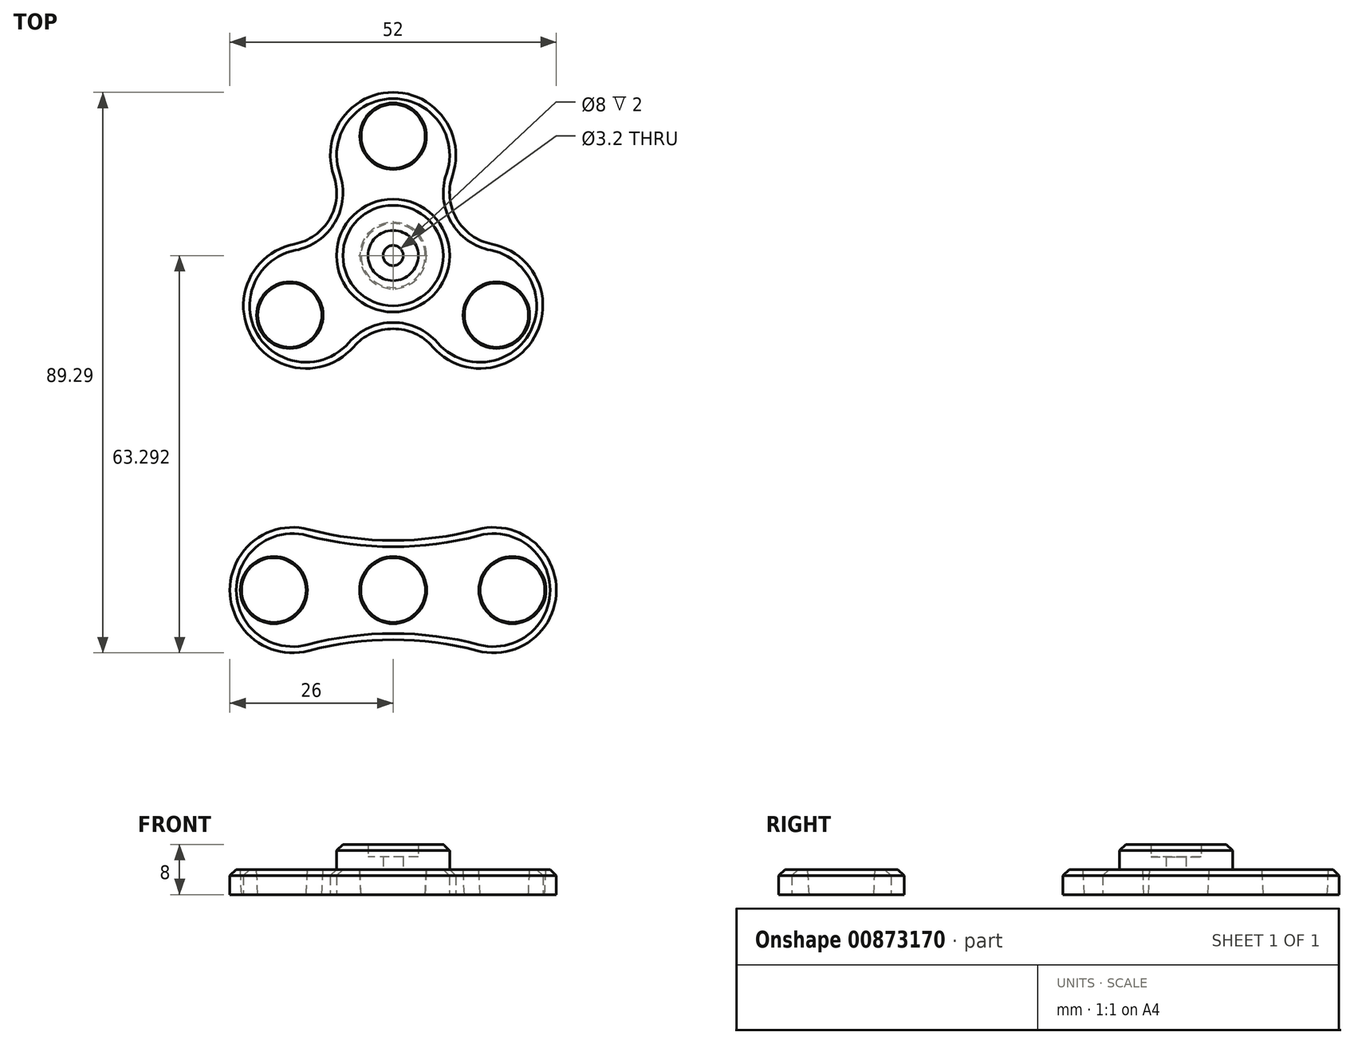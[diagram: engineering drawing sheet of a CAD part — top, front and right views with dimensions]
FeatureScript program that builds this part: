
annotation { "Feature Type Name" : "Feature", "Feature Type Description" : "" }
export const myFeature = defineFeature(function(context is Context, id is Id, definition is map)
    precondition{}
    {
        {
            var Q0;
            Q0=qCreatedBy(makeId("Top.planeOp"),FACE);
            var sketch = newSketch(context, id + "F0", { "sketchPlane" : qUnion([Q0])});
            skCircle(sketch, "E0", {"center": v(0, 0) * mm, "radius": 5.15 * mm});
            skCircle(sketch, "E1", {"center": v(0, 0) * mm, "radius": 30 * mm, "construction": true});
            skCircle(sketch, "E2", {"center": v(0, 0) * mm, "radius": 16 * mm, "construction": true});
            skCircle(sketch, "E3", {"center": v(-16, 0) * mm, "radius": 10 * mm});
            skCircle(sketch, "E4", {"center": v(16, 0) * mm, "radius": 10 * mm});
            skCircle(sketch, "E5", {"center": v(0, 0) * mm, "radius": 60 * mm, "construction": true});
            skArc(sketch, "E6", {"start": v(-46.93, 37.38) * mm, "mid": v(0, 7.9) * mm, "end": v(46.93, 37.38) * mm});
            skPoint(sketch, "E7.center.orphan", {"position": v(0, -60) * mm});
            skCircle(sketch, "E8", {"center": v(0, 0) * mm, "radius": 19 * mm, "construction": true});
            skCircle(sketch, "E9", {"center": v(-19, 0) * mm, "radius": 5.15 * mm});
            skCircle(sketch, "E10", {"center": v(19, 0) * mm, "radius": 5.15 * mm});
            skArc(sketch, "E11.MirrorCS", {"start": v(-46.93, -37.38) * mm, "mid": v(0, -7.9) * mm, "end": v(46.93, -37.38) * mm});
            skSolve(sketch);
        }
        {
            var Q0;
            Q0=makeQuery(id+"F0.imprint","IMPRINT",FACE,{"disambiguationData":[TD([[makeQuery(id+"F0.imprint","IMPRINT",EDGE,{"derivedFrom":sQuery(id+"F0.wireOp",EDGE,"kzVZ2nqX-SIj2-GYyN-E4sG-fJVBGGT2UGiY")}),-1.0]])]});
            var Q1;
            Q1=makeQuery(id+"F0.imprint","IMPRINT",FACE,{"disambiguationData":[TD([[makeQuery(id+"F0.imprint","IMPRINT",EDGE,{"derivedFrom":sQuery(id+"F0.wireOp",EDGE,"E0")}),-1.0]])]});
            var Q2;
            Q2=makeQuery(id+"F0.imprint","IMPRINT",FACE,{"disambiguationData":[TD([[makeQuery(id+"F0.imprint","IMPRINT",EDGE,{"derivedFrom":sQuery(id+"F0.wireOp",EDGE,"PU9XcHGf-sTf9-tFIX-0EHb-OrcDif7mutCM")}),-1.0]])]});
            var Q3;
            Q3=makeQuery(id+"F0.imprint","IMPRINT",FACE,{"disambiguationData":[TD([[makeQuery(id+"F0.imprint","IMPRINT",EDGE,{"derivedFrom":sQuery(id+"F0.wireOp",EDGE,"E9")}),-1.0]])]});
            var Q4;
            Q4=makeQuery(id+"F0.imprint","IMPRINT",FACE,{"disambiguationData":[TD([[makeQuery(id+"F0.imprint","IMPRINT",EDGE,{"derivedFrom":sQuery(id+"F0.wireOp",EDGE,"E10")}),-1.0]])]});
            extrude(context, id + "F1", {"entities" : qUnion([Q0, Q1, Q2, Q3, Q4]), "depth" : 4 * mm, "offsetDistance" : 25 * mm});
        }
        {
            var Q0;
            Q0=makeQuery(id+"F1.opExtrude","CAP_EDGE",EDGE,{"disambiguationData":[OSD([sQuery(id+"F0.wireOp",EDGE,"9445dba6-547d-4354-881b-b922ac0d47a12")])],"isStart":false});
            var Q1;
            Q1=makeQuery(id+"F1.opExtrude","CAP_EDGE",EDGE,{"disambiguationData":[OSD([sQuery(id+"F0.wireOp",EDGE,"E11.MirrorCS")])],"isStart":false});
            chamfer(context, id + "F2", {"entities" : qUnion([Q0, Q1]), "width" : 1 * mm, "tangentPropagation" : true});
        }
        {
            var Q0;
            Q0=qCreatedBy(makeId("Top.planeOp"),FACE);
            var sketch = newSketch(context, id + "F3", { "sketchPlane" : qUnion([Q0])});
            skCircle(sketch, "E12", {"center": v(0, 53.3) * mm, "radius": 5.1 * mm});
            skCircle(sketch, "E13", {"center": v(0, 53.3) * mm, "radius": 16 * mm, "construction": true});
            skCircle(sketch, "E14", {"center": v(0, 53.3) * mm, "radius": 19 * mm, "construction": true});
            skCircle(sketch, "E15", {"center": v(0, 69.3) * mm, "radius": 10 * mm});
            skCircle(sketch, "E16", {"center": v(0, 72.3) * mm, "radius": 5.1 * mm});
            skCircle(sketch, "E17.1.0", {"center": v(-13.86, 45.3) * mm, "radius": 10 * mm});
            skCircle(sketch, "E17.1.1", {"center": v(-16.45, 43.8) * mm, "radius": 5.1 * mm});
            skCircle(sketch, "E17.2.0", {"center": v(13.86, 45.3) * mm, "radius": 10 * mm});
            skCircle(sketch, "E17.2.1", {"center": v(16.45, 43.8) * mm, "radius": 5.1 * mm});
            skCircle(sketch, "E18", {"center": v(0, 53.3) * mm, "radius": 20 * mm, "construction": true});
            skLineSegment(sketch, "E19", {"start": v(0, 53.3) * mm, "end": v(-17.32, 63.3) * mm, "construction": true});
            skArc(sketch, "E20", {"start": v(-11.74, 69.48) * mm, "mid": v(-24.53, 67.46) * mm, "end": v(-19.9, 55.37) * mm});
            skArc(sketch, "E21", {"start": v(-19.9, 55.37) * mm, "mid": v(-10.1, 59.13) * mm, "end": v(-11.74, 69.48) * mm});
            skArc(sketch, "E22.1.0", {"start": v(8.15, 35.03) * mm, "mid": v(0, 41.62) * mm, "end": v(-8.15, 35.03) * mm});
            skArc(sketch, "E22.2.0", {"start": v(11.74, 69.48) * mm, "mid": v(10.1, 59.13) * mm, "end": v(19.9, 55.37) * mm});
            skSolve(sketch);
        }
        {
            var Q0;
            Q0=makeQuery(id+"F3.imprint","IMPRINT",FACE,{"disambiguationData":[TD([[makeQuery(id+"F3.imprint","IMPRINT",EDGE,{"derivedFrom":sQuery(id+"F3.wireOp",EDGE,"E16")}),-1.0]])]});
            var Q1;
            Q1=makeQuery(id+"F3.imprint","IMPRINT",FACE,{"disambiguationData":[TD([[makeQuery(id+"F3.imprint","IMPRINT",EDGE,{"derivedFrom":sQuery(id+"F3.wireOp",EDGE,"E12")}),-1.0]])]});
            var Q2;
            Q2=makeQuery(id+"F3.imprint","IMPRINT",FACE,{"disambiguationData":[TD([[makeQuery(id+"F3.imprint","IMPRINT",EDGE,{"derivedFrom":sQuery(id+"F3.wireOp",EDGE,"E17.2.1")}),-1.0]])]});
            var Q3;
            Q3=makeQuery(id+"F3.imprint","IMPRINT",FACE,{"disambiguationData":[TD([[makeQuery(id+"F3.imprint","IMPRINT",EDGE,{"derivedFrom":sQuery(id+"F3.wireOp",EDGE,"E17.1.1")}),-1.0]])]});
            extrude(context, id + "F4", {"entities" : qUnion([Q0, Q1, Q2, Q3]), "depth" : 4 * mm, "offsetDistance" : 25 * mm});
        }
        {
            var Q0;
            Q0=makeQuery(id+"F4.opExtrude","CAP_EDGE",EDGE,{"disambiguationData":[OSD([sQuery(id+"F3.wireOp",EDGE,"E17.1.0")])],"isStart":false});
            chamfer(context, id + "F5", {"entities" : qUnion([Q0]), "width" : 1 * mm, "tangentPropagation" : true});
        }
        {
            var Q0;
            Q0=makeQuery(id+"F1.opExtrude","CAP_EDGE",EDGE,{"disambiguationData":[OSD([sQuery(id+"F0.wireOp",EDGE,"kzVZ2nqX-SIj2-GYyN-E4sG-fJVBGGT2UGiY")])],"isStart":false});
            var Q1;
            Q1=makeQuery(id+"F1.opExtrude","CAP_EDGE",EDGE,{"disambiguationData":[OSD([sQuery(id+"F0.wireOp",EDGE,"E9")])],"isStart":false});
            var Q2;
            Q2=makeQuery(id+"F1.opExtrude","CAP_EDGE",EDGE,{"disambiguationData":[OSD([sQuery(id+"F0.wireOp",EDGE,"E10")])],"isStart":false});
            var Q3;
            Q3=makeQuery(id+"F1.opExtrude","CAP_EDGE",EDGE,{"disambiguationData":[OSD([sQuery(id+"F0.wireOp",EDGE,"E0")])],"isStart":false});
            var Q4;
            Q4=makeQuery(id+"F4.opExtrude","CAP_EDGE",EDGE,{"disambiguationData":[OSD([sQuery(id+"F3.wireOp",EDGE,"E17.1.1")])],"isStart":false});
            var Q5;
            Q5=makeQuery(id+"F4.opExtrude","CAP_EDGE",EDGE,{"disambiguationData":[OSD([sQuery(id+"F3.wireOp",EDGE,"E12")])],"isStart":false});
            var Q6;
            Q6=makeQuery(id+"F4.opExtrude","CAP_EDGE",EDGE,{"disambiguationData":[OSD([sQuery(id+"F3.wireOp",EDGE,"E16")])],"isStart":false});
            var Q7;
            Q7=makeQuery(id+"F4.opExtrude","CAP_EDGE",EDGE,{"disambiguationData":[OSD([sQuery(id+"F3.wireOp",EDGE,"E17.2.1")])],"isStart":false});
            chamfer(context, id + "F6", {"entities" : qUnion([Q0, Q1, Q2, Q3, Q4, Q5, Q6, Q7]), "chamferType" : ChamferType.TWO_OFFSETS, "width1" : 4 * mm, "oppositeDirection" : false, "width2" : 0.2 * mm, "tangentPropagation" : true});
        }
        {
            var Q0;
            Q0=makeQuery(id+"F4.opExtrude","CAP_FACE",FACE,{"disambiguationData":[OSD([sQuery(id+"F3.wireOp",EDGE,"E12"),sQuery(id+"F3.wireOp",EDGE,"E15"),sQuery(id+"F3.wireOp",EDGE,"E16"),sQuery(id+"F3.wireOp",EDGE,"E17.1.0"),sQuery(id+"F3.wireOp",EDGE,"E17.1.1"),sQuery(id+"F3.wireOp",EDGE,"E17.2.0"),sQuery(id+"F3.wireOp",EDGE,"E17.2.1"),sQuery(id+"F3.wireOp",EDGE,"E21"),sQuery(id+"F3.wireOp",EDGE,"E22.1.0"),sQuery(id+"F3.wireOp",EDGE,"E22.2.0")])],"isStart":false});
            var sketch = newSketch(context, id + "F7", { "sketchPlane" : qUnion([Q0])});
            skCircle(sketch, "E23", {"center": v(0, 53.3) * mm, "radius": 9 * mm});
            skCircle(sketch, "E24", {"center": v(0, 53.3) * mm, "radius": 1.6 * mm});
            skCircle(sketch, "E25", {"center": v(0, 53.3) * mm, "radius": 4 * mm});
            skSolve(sketch);
        }
        {
            var Q0;
            Q0=makeQuery(id+"F7.imprint","IMPRINT",FACE,{"disambiguationData":[TD([[makeQuery(id+"F7.imprint","IMPRINT",EDGE,{"derivedFrom":sQuery(id+"F7.wireOp",EDGE,"E23")}),1.0]])]});
            var Q1;
            Q1=makeQuery(id+"F7.imprint","IMPRINT",FACE,{"disambiguationData":[TD([[makeQuery(id+"F7.imprint","IMPRINT",EDGE,{"derivedFrom":sQuery(id+"F7.wireOp",EDGE,"E25")}),-1.0]])]});
            extrude(context, id + "F8", {"entities" : qUnion([Q0, Q1]), "depth" : 4 * mm, "offsetDistance" : 25 * mm});
        }
        {
            var Q0;
            Q0=makeQuery(id+"F7.imprint","IMPRINT",FACE,{"disambiguationData":[TD([[makeQuery(id+"F7.imprint","IMPRINT",EDGE,{"derivedFrom":sQuery(id+"F7.wireOp",EDGE,"E24")}),-1.0]])]});
            extrude(context, id + "F9", {"entities" : qUnion([Q0]), "operationType" : NewBodyOperationType.ADD, "depth" : 2 * mm, "offsetDistance" : 25 * mm});
        }
        {
            var Q0;
            Q0=makeQuery(id+"F8.opExtrude","CAP_EDGE",EDGE,{"disambiguationData":[OSD([sQuery(id+"F7.wireOp",EDGE,"E23")])],"isStart":false});
            chamfer(context, id + "F10", {"entities" : qUnion([Q0]), "width" : 1 * mm, "tangentPropagation" : true});
        }
    });
